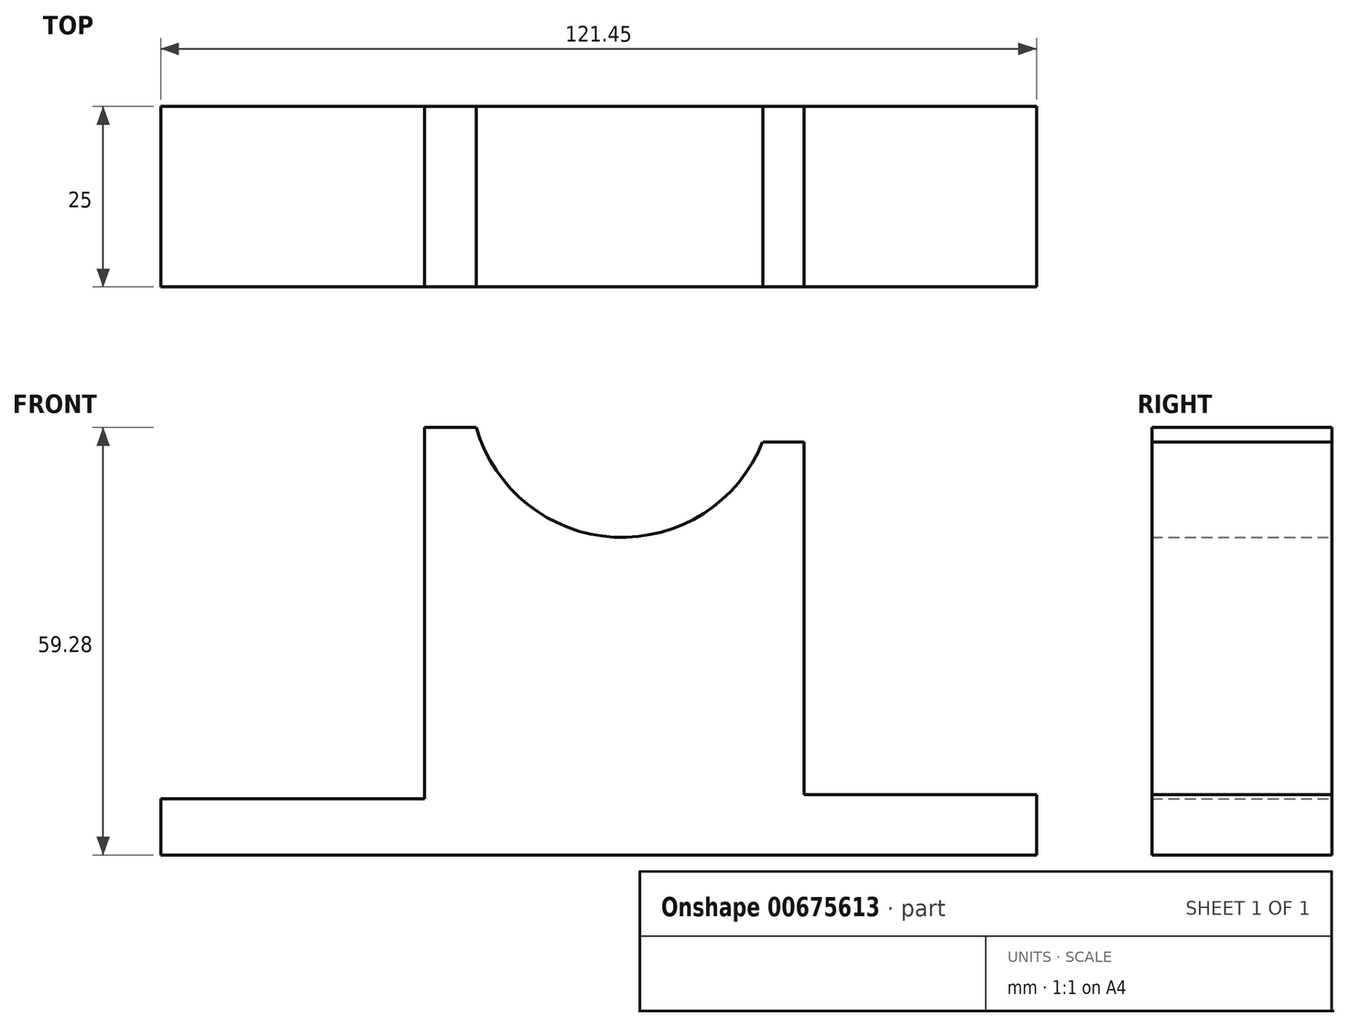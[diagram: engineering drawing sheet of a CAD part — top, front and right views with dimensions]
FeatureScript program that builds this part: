
annotation { "Feature Type Name" : "Feature", "Feature Type Description" : "" }
export const myFeature = defineFeature(function(context is Context, id is Id, definition is map)
    precondition{}
    {
        {
            var Q0;
            Q0=qCreatedBy(makeId("Front.planeOp"),FACE);
            var sketch = newSketch(context, id + "F0", { "sketchPlane" : qUnion([Q0])});
            skLineSegment(sketch, "E0", {"start": v(-55.7, -40.72) * mm, "end": v(65.76, -40.72) * mm});
            skLineSegment(sketch, "E1", {"start": v(65.76, -40.72) * mm, "end": v(65.76, -32.38) * mm});
            skLineSegment(sketch, "E2", {"start": v(65.76, -32.38) * mm, "end": v(33.53, -32.38) * mm});
            skLineSegment(sketch, "E3", {"start": v(33.53, -32.38) * mm, "end": v(33.53, 16.55) * mm});
            skLineSegment(sketch, "E4", {"start": v(33.53, 16.55) * mm, "end": v(27.77, 16.55) * mm});
            skLineSegment(sketch, "E5", {"start": v(-55.7, -40.72) * mm, "end": v(-55.7, -32.95) * mm});
            skLineSegment(sketch, "E6", {"start": v(-55.7, -32.95) * mm, "end": v(-19.14, -32.95) * mm});
            skLineSegment(sketch, "E7", {"start": v(-19.14, -32.95) * mm, "end": v(-19.14, 18.56) * mm});
            skLineSegment(sketch, "E8", {"start": v(-19.14, 18.56) * mm, "end": v(-11.94, 18.56) * mm});
            skArc(sketch, "E9", {"start": v(-11.94, 18.56) * mm, "mid": v(7.2, 3.35) * mm, "end": v(27.77, 16.55) * mm});
            skSolve(sketch);
        }
        {
            var Q0;
            Q0 = qSketchRegion(id + "F0", true);
            extrude(context, id + "F1", {"entities" : qUnion([Q0]), "depth" : 25 * mm, "offsetDistance" : 25 * mm});
        }
    });
